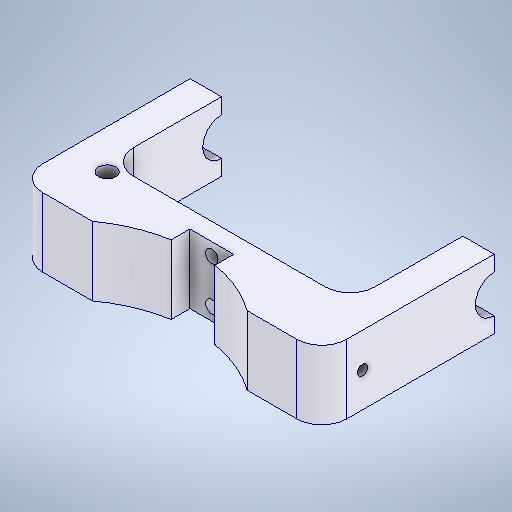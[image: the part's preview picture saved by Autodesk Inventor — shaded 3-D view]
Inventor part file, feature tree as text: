
AUTODESK INVENTOR PART (.ipt)
format: ipt  version: 2025.1 (Build 291241000, 241)  size: 342,016 bytes
history: native  units: mm
features: sketch x9, extrude x4, hole x4, mirror x2, fillet x1, projected_geometry x1
ambient origin geometry x8: Origin, YZ Plane, XZ Plane, XY Plane, X Axis, Y Axis, Z Axis, Center Point
bodies: Solid1 (feature_tree)
feature tree (21):
  extrude  "Extrusion1"  Depth=19.0mm
  extrude  "Extrusion2"  Depth=8.0mm
  extrude  "Extrusion3"  Depth=22.0mm TaperAngle=0.0deg
  hole  "Hole1"  [1 undecoded]
  extrude  "Extrusion4"  Depth=14.0mm
  mirror  "Mirror1"
  hole  "Hole2"  [1 undecoded]
  mirror  "Mirror2"
  fillet  "Fillet1"  Radius=12.5mm
  hole  "Hole3"  [1 undecoded]
  hole  "Hole4"  [1 undecoded]
  sketch  "Skizze9"  dims[d25=10.0mm d26=0.0mm d27=8.0mm d28=8.0mm d29=3.0mm d30=6.0mm d31=4.0mm d32=2.0mm d33=90.0deg d34=5.0mm d35=0.0mm d36=8.0mm d37=3.242mm d38=10.0mm d39=4.0mm d40=2.0mm d41=90.0deg d42=19.0mm d43=0.0mm d44=13.0mm d45=4.0mm d46=10.0mm d47=4.0mm d48=2.0mm d49=90.0deg d50=19.0mm d51=0.0mm d52=7.0mm d53=7.0mm d54=43.5mm d55=43.5mm]
  sketch  "Sketch1"  dims[d0=10.0mm d1=19.0mm]
  sketch  "Sketch2"  dims[d2=36.0mm d3=8.0mm]
  sketch  "Sketch3"  dims[d4=97.0mm d5=22.0mm d6=0.0mm]
  sketch  "Sketch4"  dims[d7=84.0mm d8=8.0mm]
  sketch  "Sketch5"  dims[d9=22.0mm d10=0.0mm d11=14.0mm]
  sketch  "Sketch6"  dims[d12=6.0mm d13=10.0mm d14=0.0mm]
  sketch  "Sketch7"  dims[d15=5.5mm d16=6.0mm d17=4.0mm d18=2.0mm d19=90.0deg d20=8.0mm d21=0.0mm d22=12.5mm]
  sketch  "Sketch8"  dims[d23=16.0mm d24=12.0mm]
  projected_geometry  "Projizierte Kontur1"
note: 4 required parameter values undecoded (feature->parameter linkage not recoverable at this tier; creation-order binding heuristic only, values carry confidence <= 0.55)
